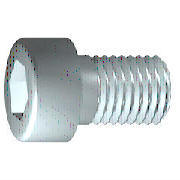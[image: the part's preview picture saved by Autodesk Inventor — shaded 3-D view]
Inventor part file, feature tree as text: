
AUTODESK INVENTOR PART (.ipt)
format: ipt  version: 2021.4 (Build 254397000, 397)  size: 198,656 bytes
history: native  units: mm (DEFAULTED — no unit token found)
features: sketch x2, extrude x1, plane x1, fillet x1
ambient origin geometry x7: Origin, YZ Plane, XY Plane, X Axis, Y Axis, Z Axis, Center Point
bodies: Solid1 (feature_tree), Body (feature_tree)
feature tree (5):
  extrude  "Slot"  Depth=6.0mm
  plane  "Work Plane1"
  fillet  "Fillet2"  Radius=6.0mm
  sketch  "Sketch1"  dims[d1=7.5mm d2=0.61355mm d3=6.0mm]
  sketch  "Sketch2"  dims[d4=3.0mm d5=60.0deg d6=6.0mm d7=6.0mm d8=5.773503mm d9=10.0mm d10=90.0deg d11=10.0mm d12=0.0mm d13=7.5mm d14=0.0mm d15=0.61345mm d16=0.61345mm d17=0.6mm d19=0.0mm d26=10.0mm d27=45.0deg d28=0.0mm d29=0.0mm d30=0.1mm]
